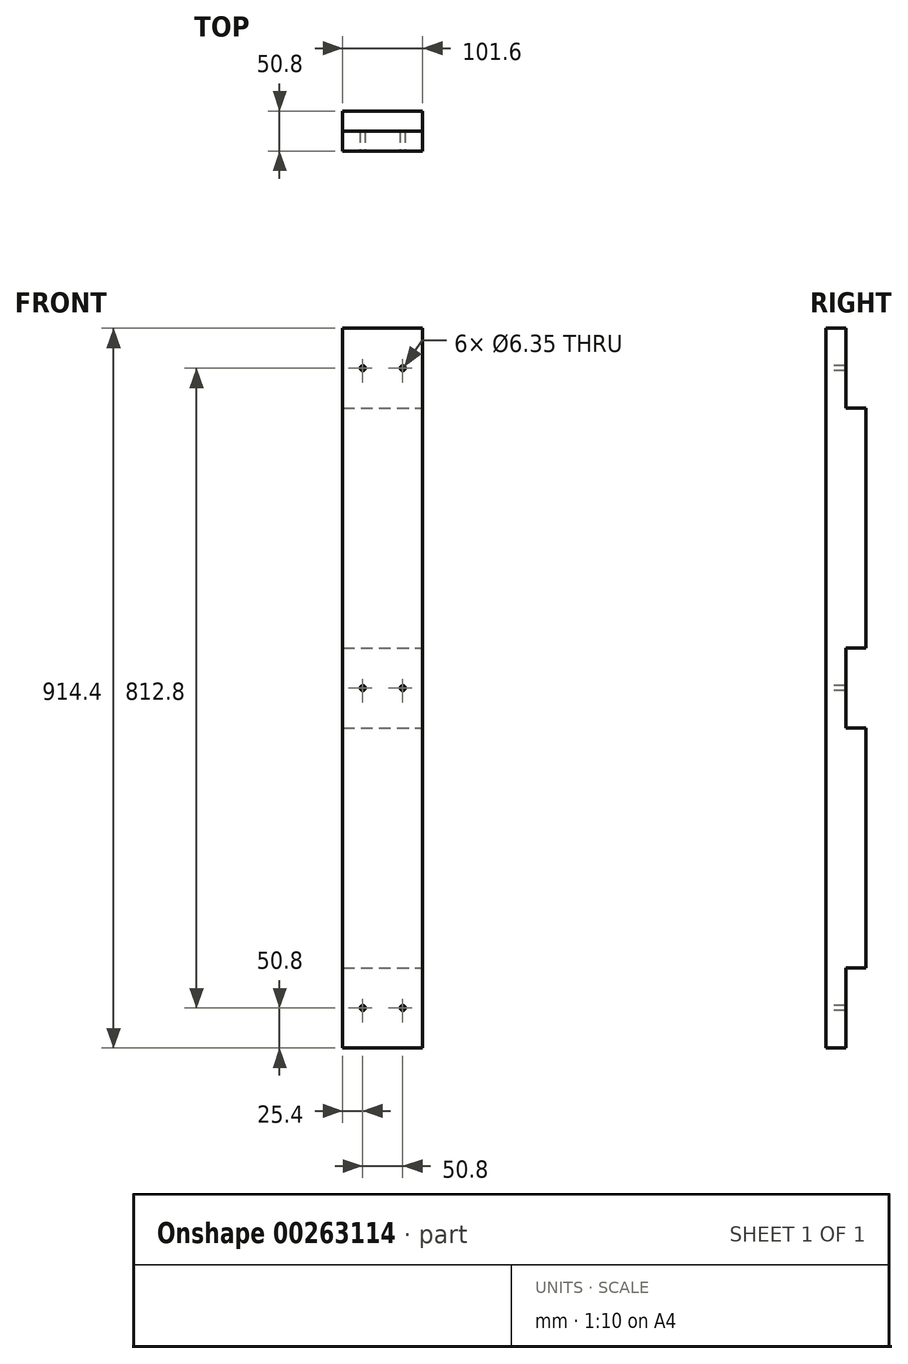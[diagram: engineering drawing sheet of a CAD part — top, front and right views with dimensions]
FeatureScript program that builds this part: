
annotation { "Feature Type Name" : "Feature", "Feature Type Description" : "" }
export const myFeature = defineFeature(function(context is Context, id is Id, definition is map)
    precondition{}
    {
        {
            var Q0;
            Q0=qCreatedBy(makeId("Top.planeOp"),FACE);
            var sketch = newSketch(context, id + "F0", { "sketchPlane" : qUnion([Q0])});
            skLineSegment(sketch, "E0.bottom", {"start": v(50.8, 25.4) * mm, "end": v(-50.8, 25.4) * mm});
            skLineSegment(sketch, "E0.top", {"start": v(50.8, -25.4) * mm, "end": v(-50.8, -25.4) * mm});
            skLineSegment(sketch, "E0.left", {"start": v(50.8, 25.4) * mm, "end": v(50.8, -25.4) * mm});
            skLineSegment(sketch, "E0.right", {"start": v(-50.8, 25.4) * mm, "end": v(-50.8, -25.4) * mm});
            skPoint(sketch, "E0.middle", {"position": v(0, 0) * mm});
            skSolve(sketch);
        }
        {
            var Q0;
            Q0=qSketchRegion(id+"F0",true);
            extrude(context, id + "F1", {"entities" : qUnion([Q0]), "depth" : 914.4 * mm});
        }
        {
            var Q0;
            Q0=makeQuery(id+"F1.opExtrude","SWEPT_FACE",FACE,{"disambiguationData":[OSD([sQuery(id+"F0.wireOp",EDGE,"E0.left")])]});
            var sketch = newSketch(context, id + "F2", { "sketchPlane" : qUnion([Q0])});
            skLineSegment(sketch, "E1.bottom", {"start": v(0, 406.4) * mm, "end": v(25.4, 406.4) * mm});
            skLineSegment(sketch, "E1.top", {"start": v(0, 508) * mm, "end": v(25.4, 508) * mm});
            skLineSegment(sketch, "E1.left", {"start": v(0, 406.4) * mm, "end": v(0, 508) * mm});
            skLineSegment(sketch, "E1.right", {"start": v(25.4, 406.4) * mm, "end": v(25.4, 508) * mm});
            skLineSegment(sketch, "E2.bottom", {"start": v(0, 101.6) * mm, "end": v(25.4, 101.6) * mm});
            skLineSegment(sketch, "E2.top", {"start": v(0, 0) * mm, "end": v(25.4, 0) * mm});
            skLineSegment(sketch, "E2.left", {"start": v(0, 101.6) * mm, "end": v(0, 0) * mm});
            skLineSegment(sketch, "E2.right", {"start": v(25.4, 101.6) * mm, "end": v(25.4, 0) * mm});
            skPoint(sketch, "E3.oppositeSnap0", {"position": v(0, 914.4) * mm});
            skLineSegment(sketch, "E3.bottom", {"start": v(25.4, 914.4) * mm, "end": v(0, 914.4) * mm});
            skLineSegment(sketch, "E3.top", {"start": v(25.4, 812.8) * mm, "end": v(0, 812.8) * mm});
            skLineSegment(sketch, "E3.left", {"start": v(25.4, 914.4) * mm, "end": v(25.4, 812.8) * mm});
            skLineSegment(sketch, "E3.right", {"start": v(0, 914.4) * mm, "end": v(0, 812.8) * mm});
            skSolve(sketch);
        }
        {
            var Q0;
            Q0=qSketchRegion(id+"F2",true);
            extrude(context, id + "F3", {"entities" : qUnion([Q0]), "operationType" : NewBodyOperationType.REMOVE, "endBound" : BoundingType.THROUGH_ALL, "oppositeDirection" : true, "depth" : 25.4 * mm});
        }
        {
            var Q0;
            Q0=makeQuery(id+"F1.opExtrude","SWEPT_FACE",FACE,{"disambiguationData":[OSD([sQuery(id+"F0.wireOp",EDGE,"E0.top")])]});
            var sketch = newSketch(context, id + "F4", { "sketchPlane" : qUnion([Q0])});
            skCircle(sketch, "E4", {"center": v(-25.4, 863.6) * mm, "radius": 3.18 * mm});
            skCircle(sketch, "E5", {"center": v(-25.4, 457.2) * mm, "radius": 3.18 * mm});
            skCircle(sketch, "E6", {"center": v(-25.4, 50.8) * mm, "radius": 3.18 * mm});
            skCircle(sketch, "E7", {"center": v(25.4, 863.6) * mm, "radius": 3.18 * mm});
            skCircle(sketch, "E8", {"center": v(25.4, 457.2) * mm, "radius": 3.18 * mm});
            skCircle(sketch, "E9", {"center": v(25.4, 50.8) * mm, "radius": 3.18 * mm});
            skSolve(sketch);
        }
        {
            var Q0;
            Q0=qSketchRegion(id+"F4",true);
            extrude(context, id + "F5", {"entities" : qUnion([Q0]), "operationType" : NewBodyOperationType.REMOVE, "endBound" : BoundingType.THROUGH_ALL, "oppositeDirection" : true, "depth" : 25.4 * mm});
        }
    });
